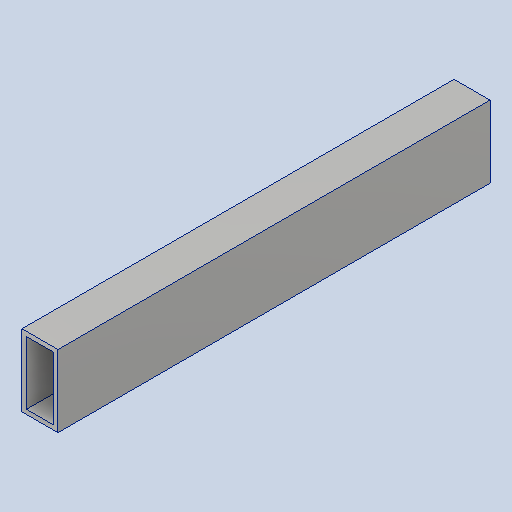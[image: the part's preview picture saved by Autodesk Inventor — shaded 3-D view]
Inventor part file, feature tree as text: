
AUTODESK INVENTOR PART (.ipt)
format: ipt  version: 2023.4 (Build 274418000, 418)  size: 229,888 bytes
history: native  units: in
note: dims shown in document units (in); Inventor stores cm internally (conversion verified against a paired STEP export)
features: extrude x1
ambient origin geometry x8: Origin, YZ Plane, XZ Plane, XY Plane, X Axis, Y Axis, Z Axis, Center Point
bodies: Solid1 (feature_tree)
feature tree (1):
  extrude  "Extrusion1"  TaperAngle=0.0deg  [1 undecoded]
note: 1 required parameter value undecoded (feature->parameter linkage not recoverable at this tier; creation-order binding heuristic only, values carry confidence <= 0.55)
